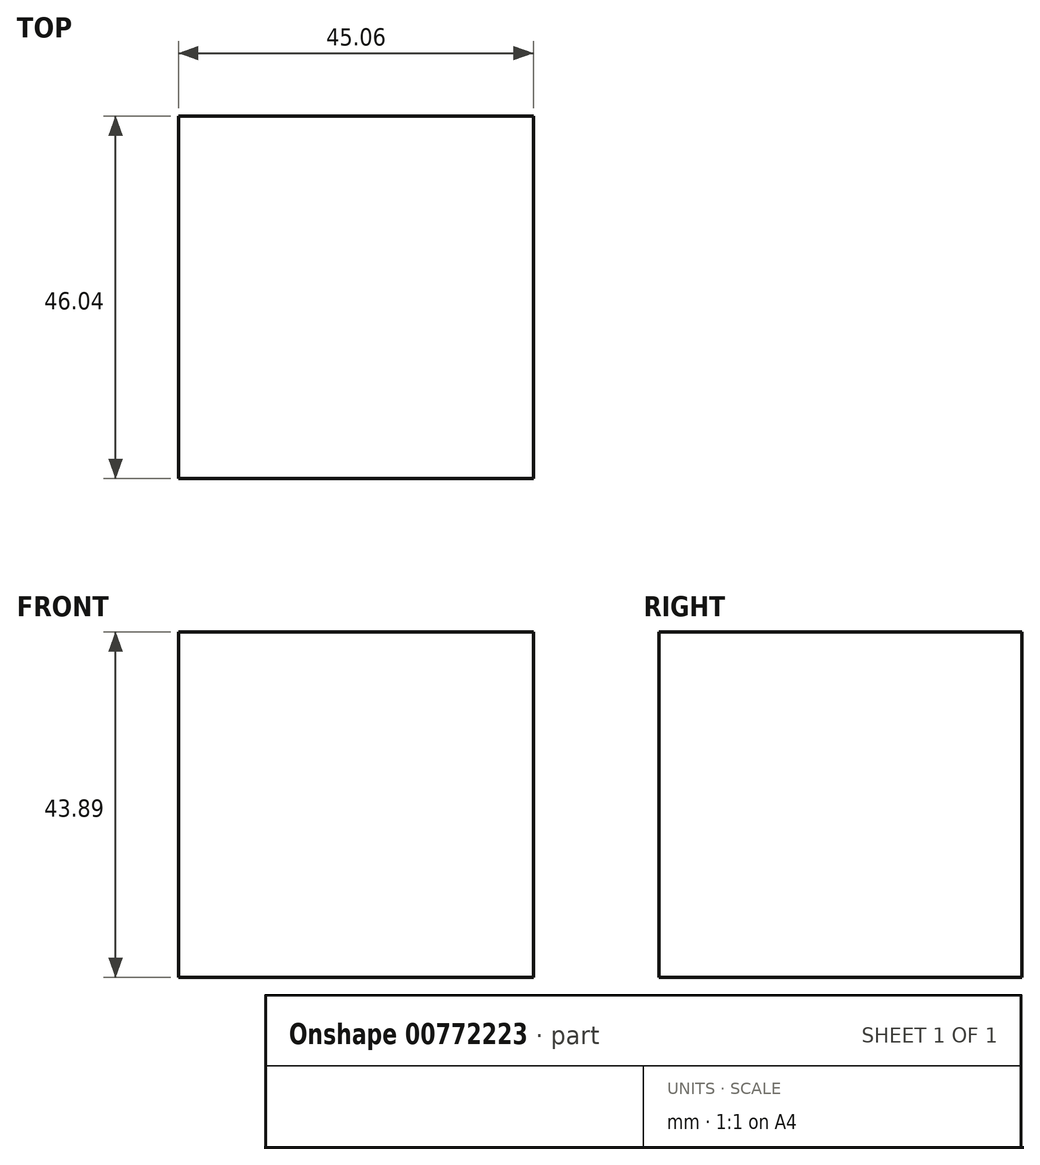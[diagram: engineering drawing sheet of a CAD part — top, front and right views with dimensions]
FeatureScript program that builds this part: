
annotation { "Feature Type Name" : "Feature", "Feature Type Description" : "" }
export const myFeature = defineFeature(function(context is Context, id is Id, definition is map)
    precondition{}
    {
        {
            var Q0;
            Q0=qCreatedBy(makeId("Front.planeOp"),FACE);
            var sketch = newSketch(context, id + "F0", { "sketchPlane" : qUnion([Q0])});
            skLineSegment(sketch, "E0.bottom", {"start": v(6.55, -47.79) * mm, "end": v(51.61, -47.79) * mm});
            skLineSegment(sketch, "E0.top", {"start": v(6.55, -91.68) * mm, "end": v(51.61, -91.68) * mm});
            skLineSegment(sketch, "E0.left", {"start": v(6.55, -47.79) * mm, "end": v(6.55, -91.68) * mm});
            skLineSegment(sketch, "E0.right", {"start": v(51.61, -47.79) * mm, "end": v(51.61, -91.68) * mm});
            skSolve(sketch);
        }
        {
            var Q0;
            Q0=makeQuery(id+"F0.imprint","IMPRINT",FACE,{"disambiguationData":[TD([[makeQuery(id+"F0.imprint","IMPRINT",EDGE,{"derivedFrom":sQuery(id+"F0.wireOp",EDGE,"E0.bottom")}),-1.0]])]});
            extrude(context, id + "F1", {"entities" : qUnion([Q0]), "depth" : 46.04 * mm, "offsetDistance" : 25.4 * mm});
        }
    });
